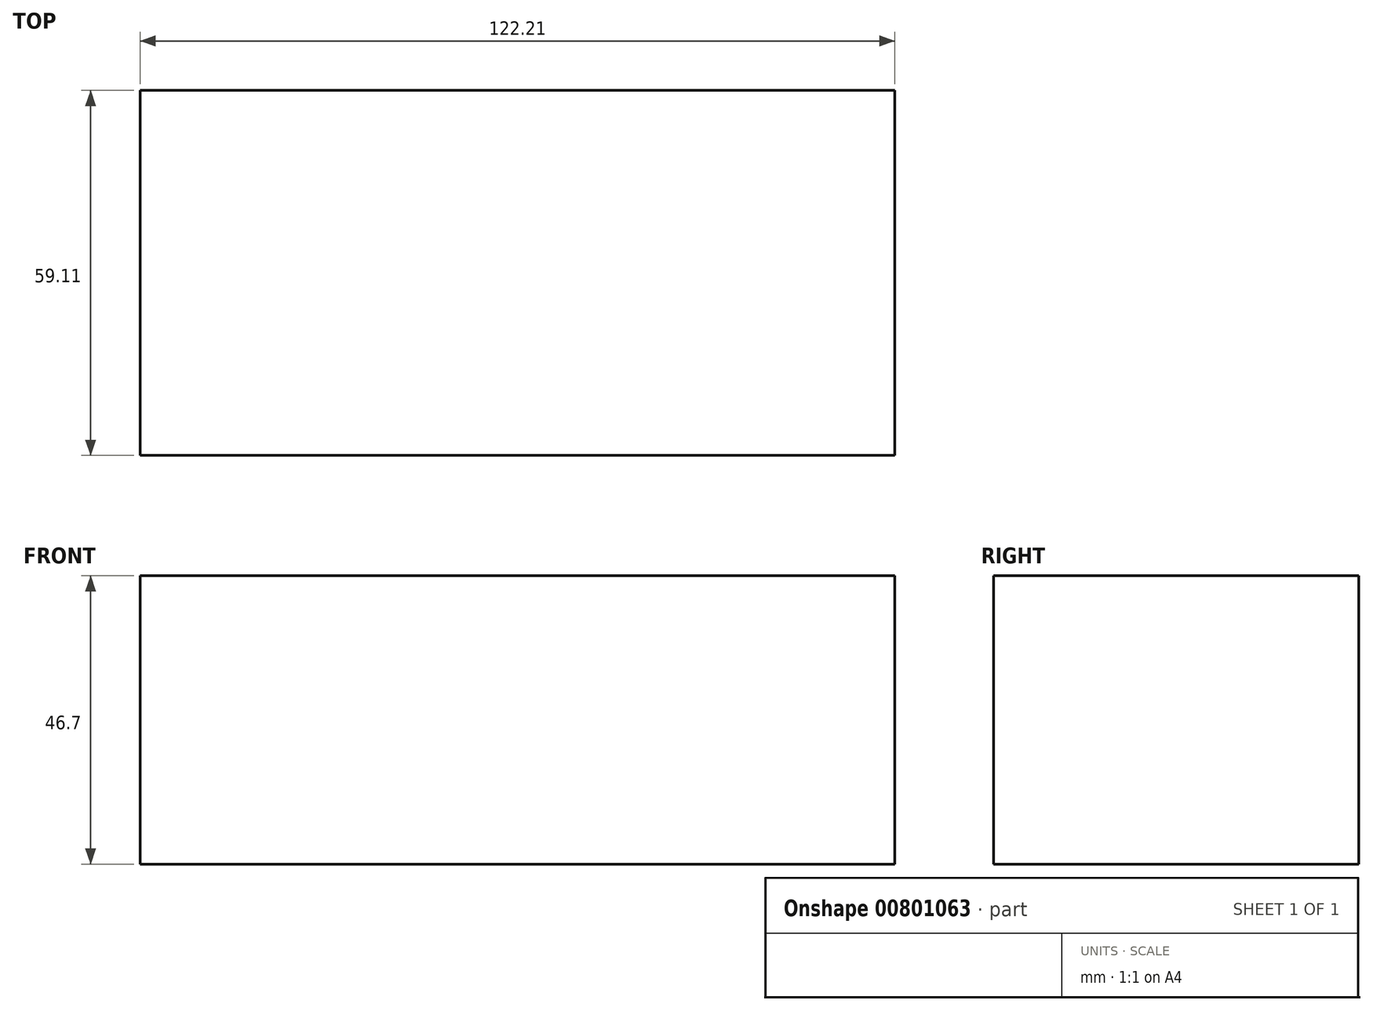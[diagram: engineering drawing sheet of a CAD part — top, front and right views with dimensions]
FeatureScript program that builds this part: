
annotation { "Feature Type Name" : "Feature", "Feature Type Description" : "" }
export const myFeature = defineFeature(function(context is Context, id is Id, definition is map)
    precondition{}
    {
        {
            var Q0;
            Q0=qCreatedBy(makeId("Top.planeOp"),FACE);
            var sketch = newSketch(context, id + "F0", { "sketchPlane" : qUnion([Q0])});
            skLineSegment(sketch, "E0.bottom", {"start": v(-65.88, 36.52) * mm, "end": v(56.33, 36.52) * mm});
            skLineSegment(sketch, "E0.top", {"start": v(-65.88, -22.59) * mm, "end": v(56.33, -22.59) * mm});
            skLineSegment(sketch, "E0.left", {"start": v(-65.88, 36.52) * mm, "end": v(-65.88, -22.59) * mm});
            skLineSegment(sketch, "E0.right", {"start": v(56.33, 36.52) * mm, "end": v(56.33, -22.59) * mm});
            skSolve(sketch);
        }
        {
            var Q0;
            Q0=makeQuery(id+"F0.imprint","IMPRINT",FACE,{"disambiguationData":[TD([[makeQuery(id+"F0.imprint","IMPRINT",EDGE,{"derivedFrom":sQuery(id+"F0.wireOp",EDGE,"E0.bottom")}),-1.0]])]});
            extrude(context, id + "F1", {"entities" : qUnion([Q0]), "depth" : 46.7 * mm, "offsetDistance" : 25 * mm});
        }
        {
            var Q0;
            Q0=makeQuery(id+"F1.opExtrude","CAP_FACE",FACE,{"disambiguationData":[OSD([sQuery(id+"F0.wireOp",EDGE,"E0.bottom"),sQuery(id+"F0.wireOp",EDGE,"E0.top"),sQuery(id+"F0.wireOp",EDGE,"E0.left"),sQuery(id+"F0.wireOp",EDGE,"E0.right")])],"isStart":false});
            var sketch = newSketch(context, id + "F2", { "sketchPlane" : qUnion([Q0])});
            skLineSegment(sketch, "E1.bottom", {"start": v(-58.38, 30.07) * mm, "end": v(49.56, 30.07) * mm});
            skLineSegment(sketch, "E1.top", {"start": v(-58.38, -16.55) * mm, "end": v(49.56, -16.55) * mm});
            skLineSegment(sketch, "E1.left", {"start": v(-58.38, 30.07) * mm, "end": v(-58.38, -16.55) * mm});
            skLineSegment(sketch, "E1.right", {"start": v(49.56, 30.07) * mm, "end": v(49.56, -16.55) * mm});
            skSolve(sketch);
        }
        {
            var Q0;
            Q0=makeQuery(id+"F2.imprint","IMPRINT",FACE,{"disambiguationData":[TD([[makeQuery(id+"F2.imprint","IMPRINT",EDGE,{"derivedFrom":sQuery(id+"F2.wireOp",EDGE,"E1.bottom")}),-1.0]])]});
            extrude(context, id + "F3", {"entities" : qUnion([Q0]), "operationType" : NewBodyOperationType.ADD, "oppositeDirection" : true, "depth" : 37.9 * mm, "offsetDistance" : 25 * mm});
        }
    });
